# Revit family: LSTE-CM
name_source: partatom
category: Lighting Fixtures
units: mm (PartAtom-declared; Revit-internal decimal feet)

## family parameters
Cut with Voids When Loaded = No
Host = Face
Light Source = Yes
OmniClass Number = 23.80.70.11
OmniClass Title = Luminaries for Internal Lighting
Part Type = Normal
Room Calculation Point = No
Round Connector Dimension = Use Diameter
Shared = No

## types (8) — shared parameters
Apparent Load = 0 VA
Backbox = White
Certifications = NYC Compliant
Color Filter = 16777215
Default Elevation = 48 "
Description = Stratus® LED Architectural Recessed
Dimming Lamp Color Temperature Shift = <None>
Emit Shape Visible in Rendering = No
Emit from Rectangle Width = 23 "
Lamp = LED Lamp
Light Bulb = White Glass
Load Classification = Lighting
Manufacturer = Columbia Lighting
Suspension Height = 48 "
Tilt Angle = 90.00°
URL = https://www.currentlighting.com
Voltage = 120 V
Warranty = Five year warranty
Wattage Comments = 24-88 W
Width = 24 "

## per-type parameters (varying)
| type | Emit from Rectangle Length | Lumen Output | Model | Nominal Watts | Photometric Web File | Row Length | zz Length |
| LSTE24-35XWG-MPO-EDU | 47 " | Extra Low Watt | LSTE24-CM | 24 W | LSTE24-35XWG-MPO-EDU.ies | 48 " | 47 " |
| LSTE24-50XLG-MPO-EDU | 47 " | Extra High Lumen | LSTE24-CM | 88 W | LSTE24-50XLG-MPO-EDU.ies | 48 " | 47 " |
| LSTE24-40LWG-MPO-EDU | 47 " | Low Watt | LSTE24-CM | 43 W | LSTE24-40LWG-MPO-EDU.ies | 48 " | 47 " |
| LSTE24-30MWG-MPO-EDU | 47 " | Medium Low Watt | LSTE24-CM | 37 W | LSTE24-30MWG-MPO-EDU.ies | 48 " | 47 " |
| LSTE22-50VLG-MPO-EDU | 23 " | Very High Lumen | LSTE22-CM | 52 W | LSTE22-50VLG-MPO-EDU.ies | 24 " | 23 " |
| LSTE22-40MLG-MPO-EDU | 23 " | Medium Lumen | LSTE22-CM | 40 W | LSTE22-40MLG-MPO-EDU.ies | 24 " | 23 " |
| LSTE22-35HLG-MPO-EDU | 23 " | High Lumen | LSTE22-CM | 42 W | LSTE22-35HLG-MPO-EDU.ies | 24 " | 23 " |
| LSTE22-30LWG-MPO-EDU | 23 " | Low Watt | LSTE22-CM | 29 W | LSTE22-30LWG-MPO-EDU.ies | 24 " | 23 " |

## geometry (parser evidence)
native form markers: Sweep x3
no freeform markers — native parametric forms only
